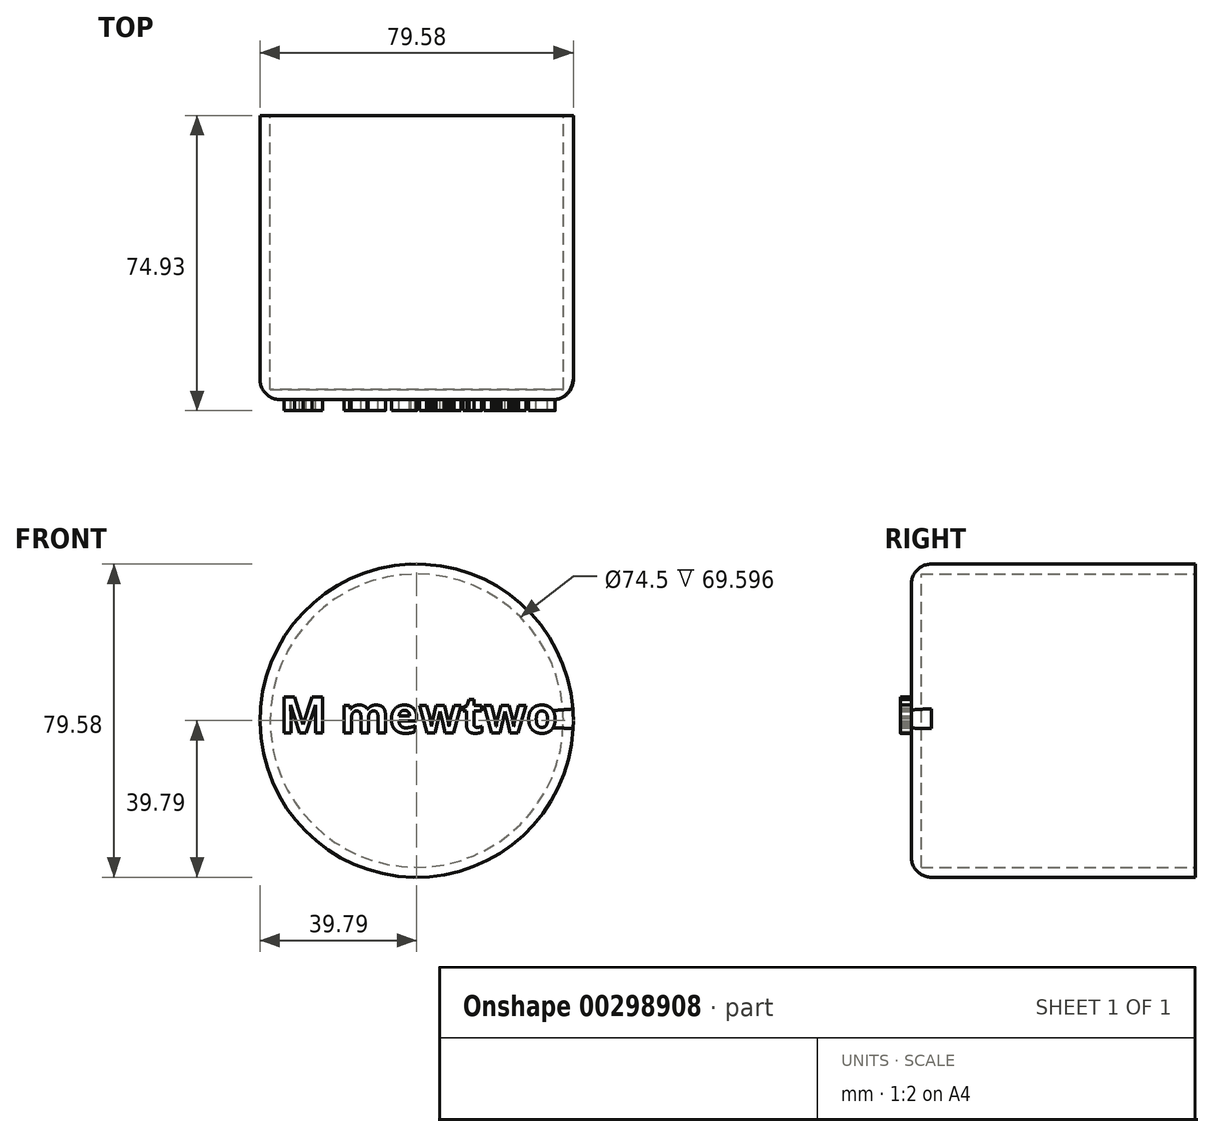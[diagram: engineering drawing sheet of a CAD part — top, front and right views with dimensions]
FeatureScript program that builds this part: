
annotation { "Feature Type Name" : "Feature", "Feature Type Description" : "" }
export const myFeature = defineFeature(function(context is Context, id is Id, definition is map)
    precondition{}
    {
        {
            var Q0;
            Q0=qCreatedBy(makeId("Front.planeOp"),FACE);
            var sketch = newSketch(context, id + "F0", { "sketchPlane" : qUnion([Q0])});
            skCircle(sketch, "E0", {"center": v(0, 0) * mm, "radius": 39.79 * mm});
            skSolve(sketch);
        }
        {
            var Q0;
            Q0=makeQuery(id+"F0.imprint","IMPRINT",FACE,{"disambiguationData":[TD([[makeQuery(id+"F0.imprint","IMPRINT",EDGE,{"derivedFrom":sQuery(id+"F0.wireOp",EDGE,"E0")}),1.0]])]});
            extrude(context, id + "F1", {"entities" : qUnion([Q0]), "depth" : 72.14 * mm});
        }
        {
            var Q0;
            Q0=qCreatedBy(makeId("Front.planeOp"),FACE);
            var sketch = newSketch(context, id + "F2", { "sketchPlane" : qUnion([Q0])});
            skText(sketch, "E1", { "text": "M mewtwo", "fontName": "OpenSans-Bold.ttf"});
            const initialGuessF2  = {"E1": [-0.03481, -0.0031, 1, 0, 0.00917]};
            skSetInitialGuess(sketch, initialGuessF2);
            skSolve(sketch);
        }
        {
            var Q0;
            Q0 = qSketchRegion(id + "F2", true);
            extrude(context, id + "F3", {"entities" : qUnion([Q0]), "operationType" : NewBodyOperationType.ADD, "depth" : 74.93 * mm});
        }
        {
            var Q0;
            Q0=makeQuery(id+"F1.opExtrude","CAP_FACE",FACE,{"disambiguationData":[OSD([sQuery(id+"F0.wireOp",EDGE,"E0")])],"isStart":true});
            shell(context, id + "F4", {"entities" : qUnion([Q0]), "thickness" : 2.54 * mm});
        }
        {
            var Q0;
            Q0=makeQuery(id+"F1.opExtrude","CAP_EDGE",EDGE,{"disambiguationData":[OSD([sQuery(id+"F0.wireOp",EDGE,"E0")])],"isStart":false});
            fillet(context, id + "F5", {"entities" : qUnion([Q0]), "radius" : 5.08 * mm, "tangentPropagation" : true, "allowEdgeOverflow" : false});
        }
    });
